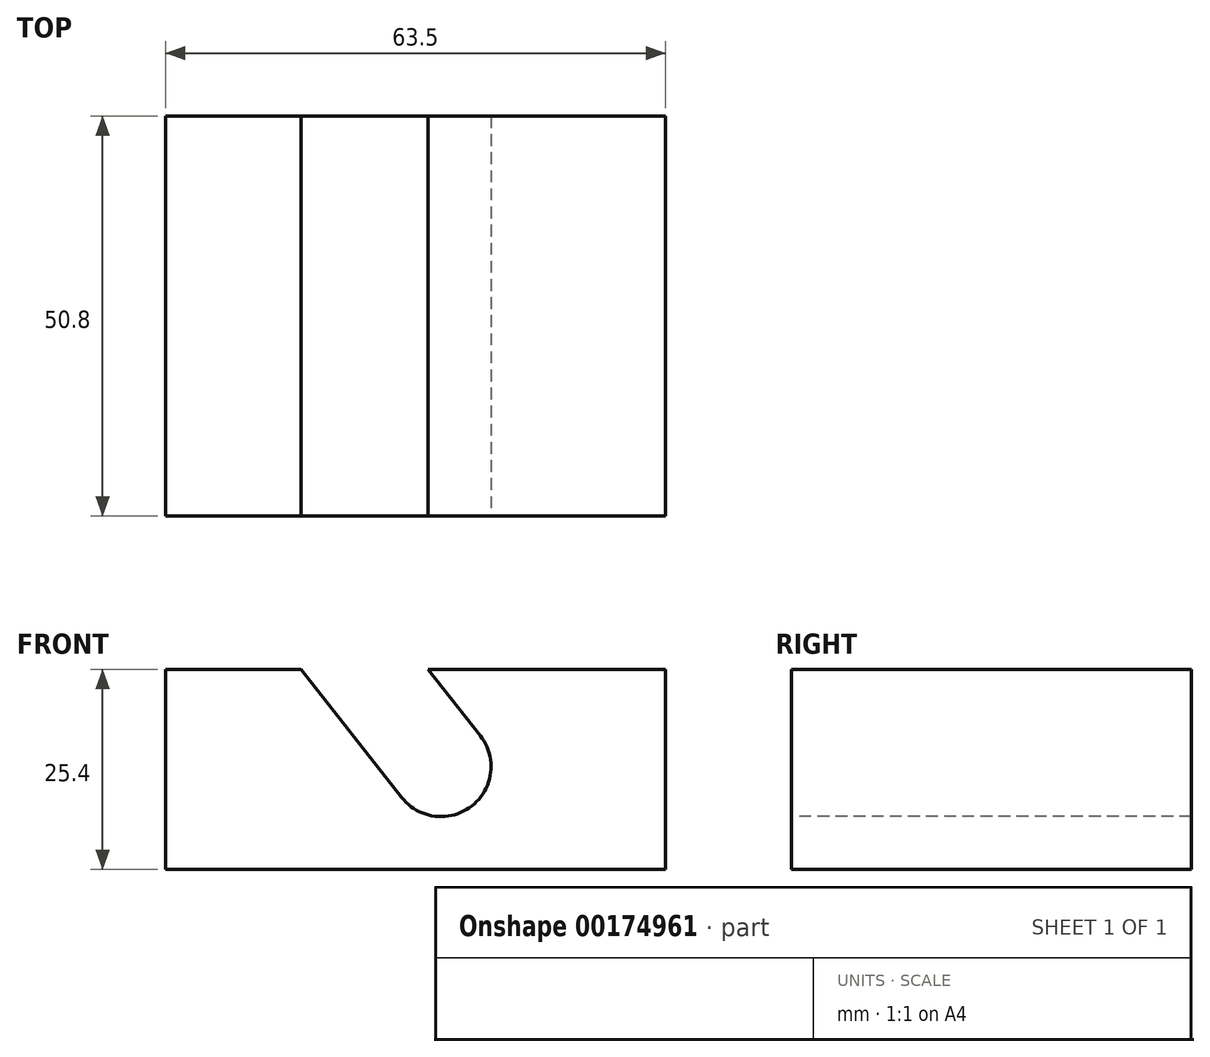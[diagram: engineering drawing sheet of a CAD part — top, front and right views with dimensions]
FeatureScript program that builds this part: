
annotation { "Feature Type Name" : "Feature", "Feature Type Description" : "" }
export const myFeature = defineFeature(function(context is Context, id is Id, definition is map)
    precondition{}
    {
        {
            var Q0;
            Q0=qCreatedBy(makeId("Top.planeOp"),FACE);
            var sketch = newSketch(context, id + "F0", { "sketchPlane" : qUnion([Q0])});
            skLineSegment(sketch, "E0.bottom", {"start": v(63.5, 25.4) * mm, "end": v(0, 25.4) * mm});
            skLineSegment(sketch, "E0.top", {"start": v(63.5, -25.4) * mm, "end": v(0, -25.4) * mm});
            skLineSegment(sketch, "E0.left", {"start": v(63.5, 25.4) * mm, "end": v(63.5, -25.4) * mm});
            skPoint(sketch, "E0.middle", {"position": v(0, 0) * mm});
            skLineSegment(sketch, "E1", {"start": v(0, 25.4) * mm, "end": v(0, -25.4) * mm});
            skPoint(sketch, "E0.right.start.orphan", {"position": v(-63.5, 25.4) * mm});
            skPoint(sketch, "E2.orphan", {"position": v(-63.5, -25.4) * mm});
            skSolve(sketch);
        }
        {
            var Q0;
            Q0 = qSketchRegion(id + "F0", true);
            extrude(context, id + "F1", {"entities" : qUnion([Q0]), "depth" : 25.4 * mm});
        }
        {
            var Q0;
            Q0=makeQuery(id+"F1.opExtrude","SWEPT_FACE",FACE,{"disambiguationData":[OSD([sQuery(id+"F0.wireOp",EDGE,"E0.top")])]});
            var sketch = newSketch(context, id + "F2", { "sketchPlane" : qUnion([Q0])});
            skArc(sketch, "E3", {"start": v(29.99, 9.14) * mm, "mid": v(38.9, 8.07) * mm, "end": v(39.97, 16.99) * mm});
            skLineSegment(sketch, "E4", {"start": v(39.97, 16.99) * mm, "end": v(33.35, 25.4) * mm});
            skLineSegment(sketch, "E5", {"start": v(29.99, 9.14) * mm, "end": v(17.2, 25.4) * mm});
            skLineSegment(sketch, "E6", {"start": v(17.2, 25.4) * mm, "end": v(33.35, 25.4) * mm});
            skSolve(sketch);
        }
        {
            var Q0;
            Q0 = qSketchRegion(id + "F2", true);
            extrude(context, id + "F3", {"entities" : qUnion([Q0]), "operationType" : NewBodyOperationType.REMOVE, "endBound" : BoundingType.THROUGH_ALL, "oppositeDirection" : true, "depth" : 25.4 * mm});
        }
    });
